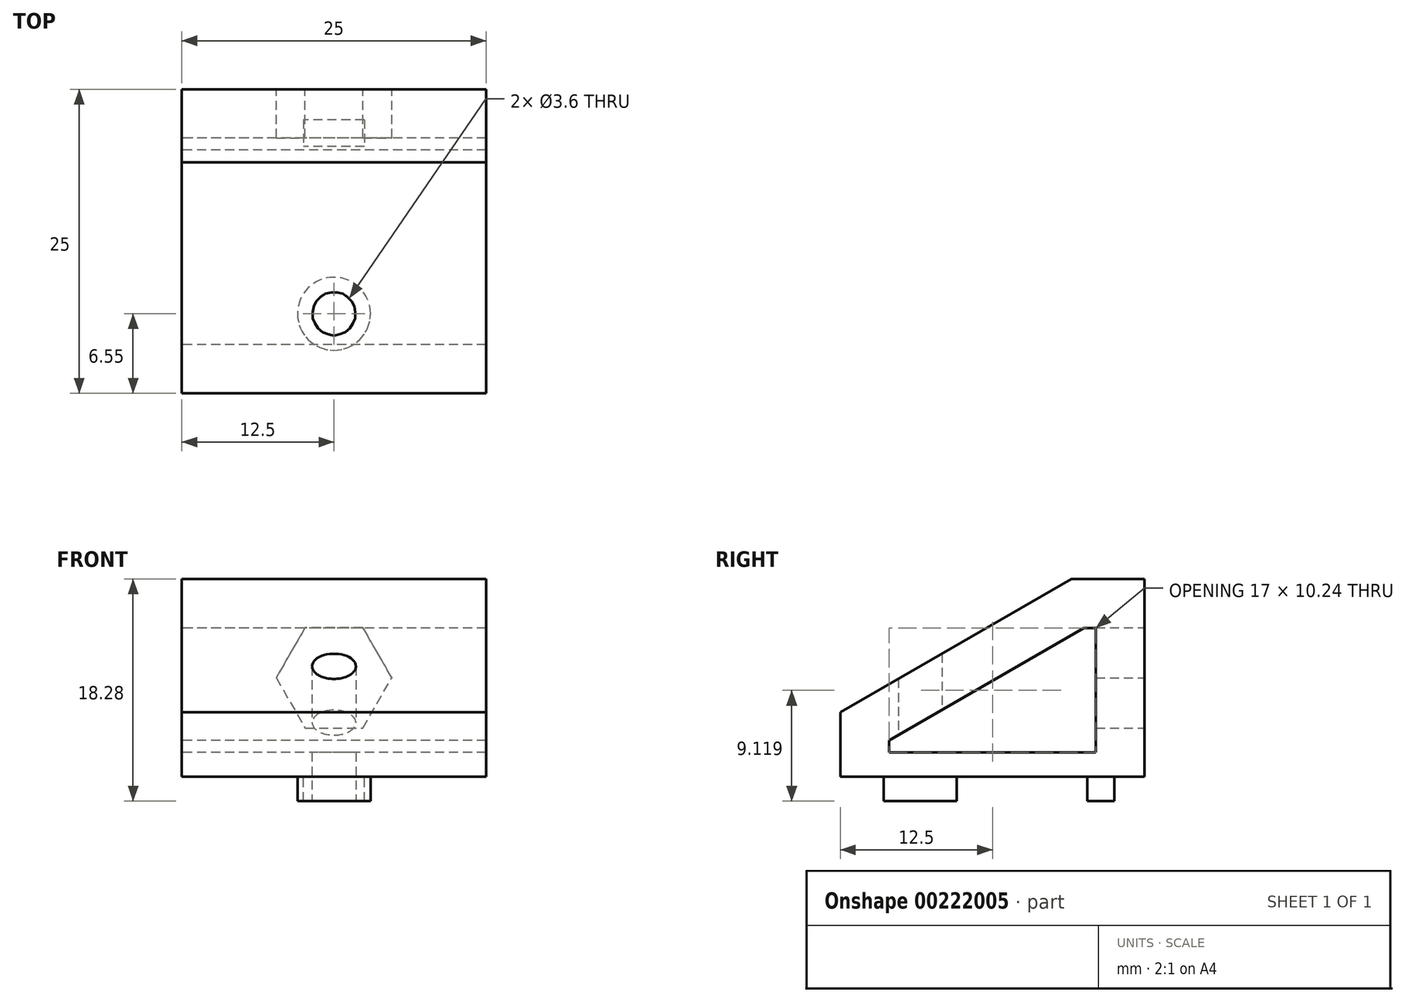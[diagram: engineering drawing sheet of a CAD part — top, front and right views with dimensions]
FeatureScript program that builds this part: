
annotation { "Feature Type Name" : "Feature", "Feature Type Description" : "" }
export const myFeature = defineFeature(function(context is Context, id is Id, definition is map)
    precondition{}
    {
        {
            var Q0;
            Q0=qCreatedBy(makeId("Top.planeOp"),FACE);
            var sketch = newSketch(context, id + "F0", { "sketchPlane" : qUnion([Q0])});
            skLineSegment(sketch, "E0.bottom", {"start": v(12.5, 12.5) * mm, "end": v(-12.5, 12.5) * mm});
            skLineSegment(sketch, "E0.top", {"start": v(12.5, -12.5) * mm, "end": v(-12.5, -12.5) * mm});
            skLineSegment(sketch, "E0.left", {"start": v(12.5, 12.5) * mm, "end": v(12.5, -12.5) * mm});
            skLineSegment(sketch, "E0.right", {"start": v(-12.5, 12.5) * mm, "end": v(-12.5, -12.5) * mm});
            skPoint(sketch, "E0.middle", {"position": v(0, 0) * mm});
            skSolve(sketch);
        }
        {
            var Q0;
            Q0 = qSketchRegion(id + "F0", true);
            extrude(context, id + "F1", {"entities" : qUnion([Q0]), "depth" : 2 * mm});
        }
        {
            var Q0;
            Q0=makeQuery(id+"F1.opExtrude","SWEPT_FACE",FACE,{"disambiguationData":[OSD([sQuery(id+"F0.wireOp",EDGE,"E0.right")])]});
            var sketch = newSketch(context, id + "F2", { "sketchPlane" : qUnion([Q0])});
            skLineSegment(sketch, "E1", {"start": v(-12.5, 2) * mm, "end": v(-12.5, 16.28) * mm});
            skLineSegment(sketch, "E2", {"start": v(-12.5, 16.28) * mm, "end": v(-6.5, 16.28) * mm});
            skLineSegment(sketch, "E3", {"start": v(-6.5, 16.28) * mm, "end": v(12.5, 5.3) * mm});
            skLineSegment(sketch, "E4", {"start": v(12.5, 5.3) * mm, "end": v(12.5, 2) * mm});
            skLineSegment(sketch, "E5", {"start": v(12.5, 2) * mm, "end": v(8.5, 2) * mm});
            skLineSegment(sketch, "E6", {"start": v(8.5, 2) * mm, "end": v(8.5, 3) * mm});
            skLineSegment(sketch, "E7", {"start": v(8.5, 3) * mm, "end": v(-7.5, 12.24) * mm});
            skLineSegment(sketch, "E8", {"start": v(-7.5, 12.24) * mm, "end": v(-8.5, 12.24) * mm});
            skLineSegment(sketch, "E9", {"start": v(-8.5, 12.24) * mm, "end": v(-8.5, 2) * mm});
            skLineSegment(sketch, "E10", {"start": v(-8.5, 2) * mm, "end": v(-12.5, 2) * mm});
            skSolve(sketch);
        }
        {
            var Q0;
            Q0 = qSketchRegion(id + "F2", true);
            var Q1;
            Q1=makeQuery(id+"F1.opExtrude","SWEPT_FACE",FACE,{"disambiguationData":[OSD([sQuery(id+"F0.wireOp",EDGE,"E0.left")])]});
            extrude(context, id + "F3", {"entities" : qUnion([Q0]), "operationType" : NewBodyOperationType.ADD, "endBound" : BoundingType.UP_TO_SURFACE, "oppositeDirection" : true, "endBoundEntityFace" : qUnion([Q1]), "depth" : 25 * mm});
        }
        {
            var Q0;
            Q0=makeQuery(id+"F1.opExtrude","CAP_FACE",FACE,{"disambiguationData":[OSD([sQuery(id+"F0.wireOp",EDGE,"E0.bottom"),sQuery(id+"F0.wireOp",EDGE,"E0.top"),sQuery(id+"F0.wireOp",EDGE,"E0.left"),sQuery(id+"F0.wireOp",EDGE,"E0.right")])],"isStart":true});
            var sketch = newSketch(context, id + "F4", { "sketchPlane" : qUnion([Q0])});
            skLineSegment(sketch, "E11.bottom", {"start": v(2.5, -10) * mm, "end": v(-2.5, -10) * mm});
            skLineSegment(sketch, "E11.top", {"start": v(2.5, -7.8) * mm, "end": v(-2.5, -7.8) * mm});
            skLineSegment(sketch, "E11.left", {"start": v(2.5, -10) * mm, "end": v(2.5, -7.8) * mm});
            skLineSegment(sketch, "E11.right", {"start": v(-2.5, -10) * mm, "end": v(-2.5, -7.8) * mm});
            skPoint(sketch, "E11.middle", {"position": v(0, -8.9) * mm});
            skCircle(sketch, "E12", {"center": v(0, 5.95) * mm, "radius": 3 * mm});
            skSolve(sketch);
        }
        {
            var Q0;
            Q0 = qSketchRegion(id + "F4", true);
            extrude(context, id + "F5", {"entities" : qUnion([Q0]), "operationType" : NewBodyOperationType.ADD, "depth" : 2 * mm});
        }
        {
            var Q0;
            Q0=makeQuery(id+"F5.opExtrude","CAP_FACE",FACE,{"disambiguationData":[OSD([sQuery(id+"F4.wireOp",EDGE,"E12")])],"isStart":false});
            var sketch = newSketch(context, id + "F6", { "sketchPlane" : qUnion([Q0])});
            skCircle(sketch, "E13", {"center": v(0, 5.95) * mm, "radius": 1.8 * mm});
            skSolve(sketch);
        }
        {
            var Q0;
            Q0 = qSketchRegion(id + "F6", true);
            extrude(context, id + "F7", {"entities" : qUnion([Q0]), "operationType" : NewBodyOperationType.REMOVE, "endBound" : BoundingType.THROUGH_ALL, "oppositeDirection" : true, "depth" : 25 * mm});
        }
        {
            var Q0;
            Q0=makeQuery(id+"F3.boolean.opBoolean","MERGE",FACE,{"derivedFrom":[makeQuery(id+"F1.opExtrude","SWEPT_FACE",FACE,{"disambiguationData":[OSD([sQuery(id+"F0.wireOp",EDGE,"E0.bottom")])]}),makeQuery(id+"F3.opExtrude","SWEPT_FACE",FACE,{"disambiguationData":[OSD([sQuery(id+"F2.wireOp",EDGE,"E1")])]})]});
            var sketch = newSketch(context, id + "F8", { "sketchPlane" : qUnion([Q0])});
            skCircle(sketch, "E14.cCircle", {"center": v(0, 8.14) * mm, "radius": 4.75 * mm, "construction": true});
            skPoint(sketch, "E14.cCircle.centerSnap0", {"position": v(12.5, 8.14) * mm});
            skPoint(sketch, "E14.cCircle.perimeterSnap0", {"position": v(12.5, 8.14) * mm});
            skLineSegment(sketch, "E14.0", {"start": v(4.75, 8.14) * mm, "end": v(2.37, 4.03) * mm});
            skPoint(sketch, "E14.0.startSnap0", {"position": v(12.5, 8.14) * mm});
            skLineSegment(sketch, "E14.1", {"start": v(2.37, 4.03) * mm, "end": v(-2.37, 4.03) * mm});
            skLineSegment(sketch, "E14.2", {"start": v(-2.37, 4.03) * mm, "end": v(-4.75, 8.14) * mm});
            skLineSegment(sketch, "E14.3", {"start": v(-4.75, 8.14) * mm, "end": v(-2.37, 12.25) * mm});
            skLineSegment(sketch, "E14.4", {"start": v(-2.37, 12.25) * mm, "end": v(2.37, 12.25) * mm});
            skLineSegment(sketch, "E14.5", {"start": v(2.37, 12.25) * mm, "end": v(4.75, 8.14) * mm});
            skSolve(sketch);
        }
        {
            var Q0;
            Q0 = qSketchRegion(id + "F8", true);
            var Q1;
            Q1=makeQuery(id+"F3.opExtrude","SWEPT_FACE",FACE,{"disambiguationData":[OSD([sQuery(id+"F2.wireOp",EDGE,"E9")])]});
            extrude(context, id + "F9", {"entities" : qUnion([Q0]), "operationType" : NewBodyOperationType.REMOVE, "endBound" : BoundingType.UP_TO_SURFACE, "oppositeDirection" : true, "endBoundEntityFace" : qUnion([Q1]), "depth" : 25 * mm});
        }
    });
